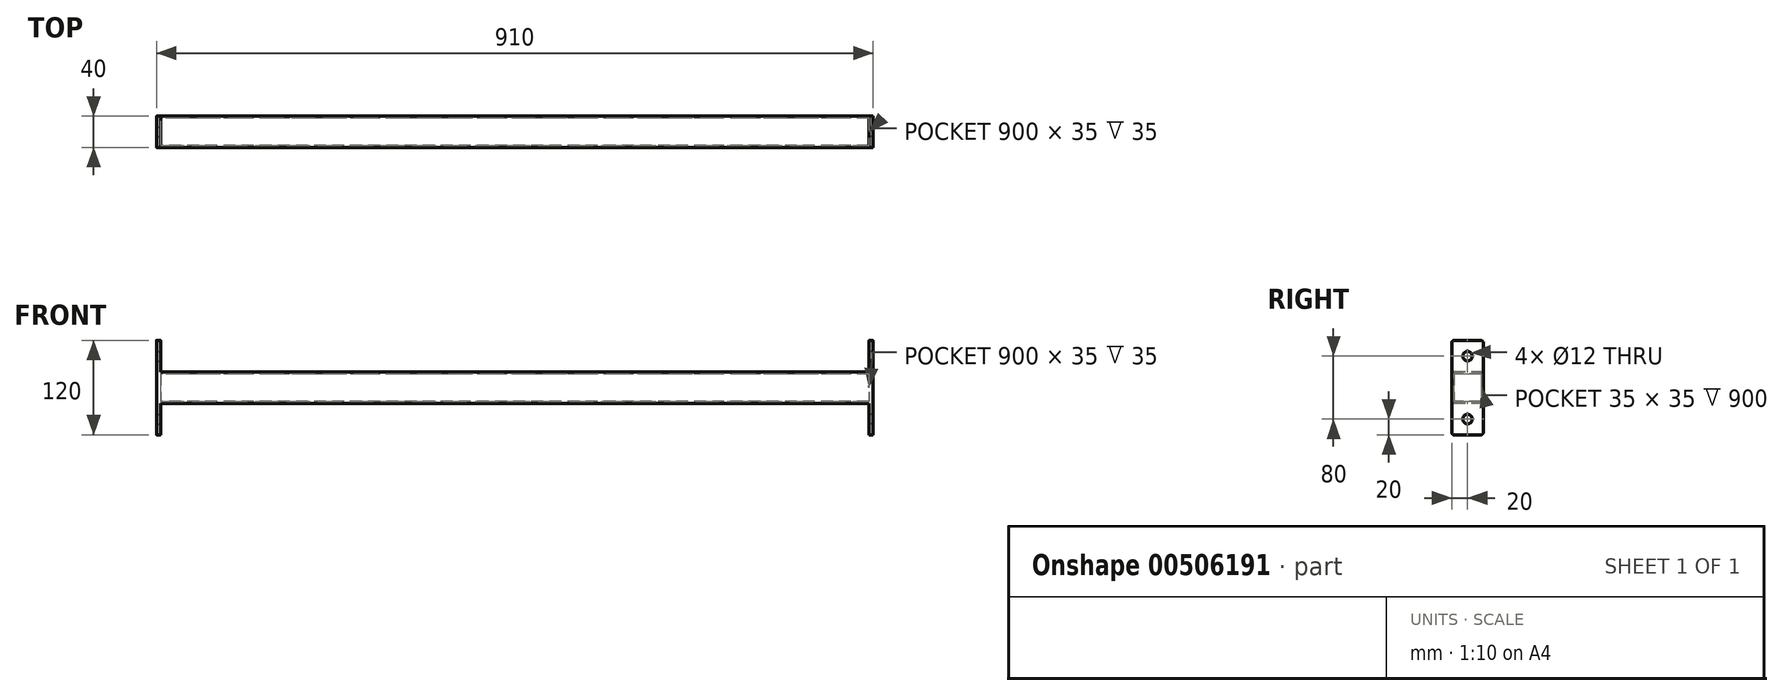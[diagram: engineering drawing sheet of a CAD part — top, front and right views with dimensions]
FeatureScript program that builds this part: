
annotation { "Feature Type Name" : "Feature", "Feature Type Description" : "" }
export const myFeature = defineFeature(function(context is Context, id is Id, definition is map)
    precondition{}
    {
        {
            var Q0;
            Q0=qCreatedBy(makeId("Right.planeOp"),FACE);
            var sketch = newSketch(context, id + "F0", { "sketchPlane" : qUnion([Q0])});
            skLineSegment(sketch, "E0.bottom", {"start": v(20, 20) * mm, "end": v(-20, 20) * mm});
            skLineSegment(sketch, "E0.top", {"start": v(20, -20) * mm, "end": v(-20, -20) * mm});
            skLineSegment(sketch, "E0.left", {"start": v(20, 20) * mm, "end": v(20, -20) * mm});
            skLineSegment(sketch, "E0.right", {"start": v(-20, 20) * mm, "end": v(-20, -20) * mm});
            skPoint(sketch, "E0.middle", {"position": v(0, 0) * mm});
            skLineSegment(sketch, "E1.bottom", {"start": v(17.5, 17.5) * mm, "end": v(-17.5, 17.5) * mm});
            skLineSegment(sketch, "E1.top", {"start": v(17.5, -17.5) * mm, "end": v(-17.5, -17.5) * mm});
            skLineSegment(sketch, "E1.left", {"start": v(17.5, 17.5) * mm, "end": v(17.5, -17.5) * mm});
            skLineSegment(sketch, "E1.right", {"start": v(-17.5, 17.5) * mm, "end": v(-17.5, -17.5) * mm});
            skSolve(sketch);
        }
        {
            var Q0;
            Q0=makeQuery(id+"F0.imprint","IMPRINT",FACE,{"disambiguationData":[TD([[makeQuery(id+"F0.imprint","IMPRINT",EDGE,{"derivedFrom":sQuery(id+"F0.wireOp",EDGE,"E0.bottom")}),1.0]])]});
            extrude(context, id + "F1", {"entities" : qUnion([Q0]), "endBound" : BoundingType.SYMMETRIC, "depth" : 900 * mm, "offsetDistance" : 25 * mm});
        }
        {
            var Q0;
            Q0=makeQuery(id+"F1.opExtrude","CAP_FACE",FACE,{"disambiguationData":[OSD([sQuery(id+"F0.wireOp",EDGE,"E0.bottom"),sQuery(id+"F0.wireOp",EDGE,"E0.top"),sQuery(id+"F0.wireOp",EDGE,"E0.left"),sQuery(id+"F0.wireOp",EDGE,"E0.right"),sQuery(id+"F0.wireOp",EDGE,"E1.bottom"),sQuery(id+"F0.wireOp",EDGE,"E1.top"),sQuery(id+"F0.wireOp",EDGE,"E1.left"),sQuery(id+"F0.wireOp",EDGE,"E1.right")])],"isStart":false});
            var sketch = newSketch(context, id + "F2", { "sketchPlane" : qUnion([Q0])});
            skLineSegment(sketch, "E2.bottom", {"start": v(20, 20) * mm, "end": v(-20, 20) * mm});
            skLineSegment(sketch, "E2.top", {"start": v(17, -60) * mm, "end": v(-17, -60) * mm});
            skLineSegment(sketch, "E2.left", {"start": v(20, 20) * mm, "end": v(20, -57) * mm});
            skLineSegment(sketch, "E2.right", {"start": v(-20, 20) * mm, "end": v(-20, -57) * mm});
            skLineSegment(sketch, "E3.left", {"start": v(20, 20) * mm, "end": v(20, -20) * mm});
            skCircle(sketch, "E4", {"center": v(0, -40) * mm, "radius": 6 * mm});
            skPoint(sketch, "E4.centerSnap0", {"position": v(0, -60) * mm});
            skPoint(sketch, "E5.visualSharp", {"position": v(-20, -60) * mm});
            skArc(sketch, "E5.filletArc", {"start": v(-20, -57) * mm, "mid": v(-19.12, -59.12) * mm, "end": v(-17, -60) * mm});
            skPoint(sketch, "E6.visualSharp", {"position": v(20, -60) * mm});
            skArc(sketch, "E6.filletArc", {"start": v(17, -60) * mm, "mid": v(19.12, -59.12) * mm, "end": v(20, -57) * mm});
            skCircle(sketch, "E7.MirrorC", {"center": v(0, 40) * mm, "radius": 6 * mm});
            skLineSegment(sketch, "E8.MirrorCS", {"start": v(-20, -20) * mm, "end": v(-20, 57) * mm});
            skLineSegment(sketch, "E9.MirrorCS", {"start": v(17, 60) * mm, "end": v(-17, 60) * mm});
            skLineSegment(sketch, "E10.MirrorCS", {"start": v(20, -20) * mm, "end": v(20, 57) * mm});
            skArc(sketch, "E11.MirrorCS", {"start": v(17, 60) * mm, "mid": v(19.12, 59.12) * mm, "end": v(20, 57) * mm});
            skArc(sketch, "E12.MirrorCS", {"start": v(-20, 57) * mm, "mid": v(-19.12, 59.12) * mm, "end": v(-17, 60) * mm});
            skSolve(sketch);
        }
        {
            var Q0;
            Q0=qSketchRegion(id+"F2",true);
            extrude(context, id + "F3", {"entities" : qUnion([Q0]), "depth" : 5 * mm});
        }
        {
            var Q0;
            Q0=makeQuery(id+"F3.opExtrude","SWEPT_BODY",BODY,{"disambiguationData":[OSD([sQuery(id+"F2.wireOp",EDGE,"E2.top"),sQuery(id+"F2.wireOp",EDGE,"E2.left"),sQuery(id+"F2.wireOp",EDGE,"E2.right"),sQuery(id+"F2.wireOp",EDGE,"E3.bottom"),sQuery(id+"F2.wireOp",EDGE,"E3.top"),sQuery(id+"F2.wireOp",EDGE,"E3.left"),sQuery(id+"F2.wireOp",EDGE,"E3.right"),sQuery(id+"F2.wireOp",EDGE,"gTgGaeDv-OfJh-3z9d-mSEW-kqISW2qM0Zl8"),sQuery(id+"F2.wireOp",EDGE,"E4"),sQuery(id+"F2.wireOp",EDGE,"d7060350-439c-4211-ad83-2698a1f480e9.filletArc"),sQuery(id+"F2.wireOp",EDGE,"1f8af891-f8d6-47e9-a65d-fee356d0fddc.filletArc"),sQuery(id+"F2.wireOp",EDGE,"E5.filletArc"),sQuery(id+"F2.wireOp",EDGE,"E6.filletArc")])]});
            var Q1;
            Q1=qCreatedBy(makeId("Right.planeOp"),FACE);
            mirror(context, id + "F4", {"operationType" : NewBodyOperationType.ADD, "entities" : qUnion([Q0]), "mirrorPlane" : qUnion([Q1])});
        }
    });
